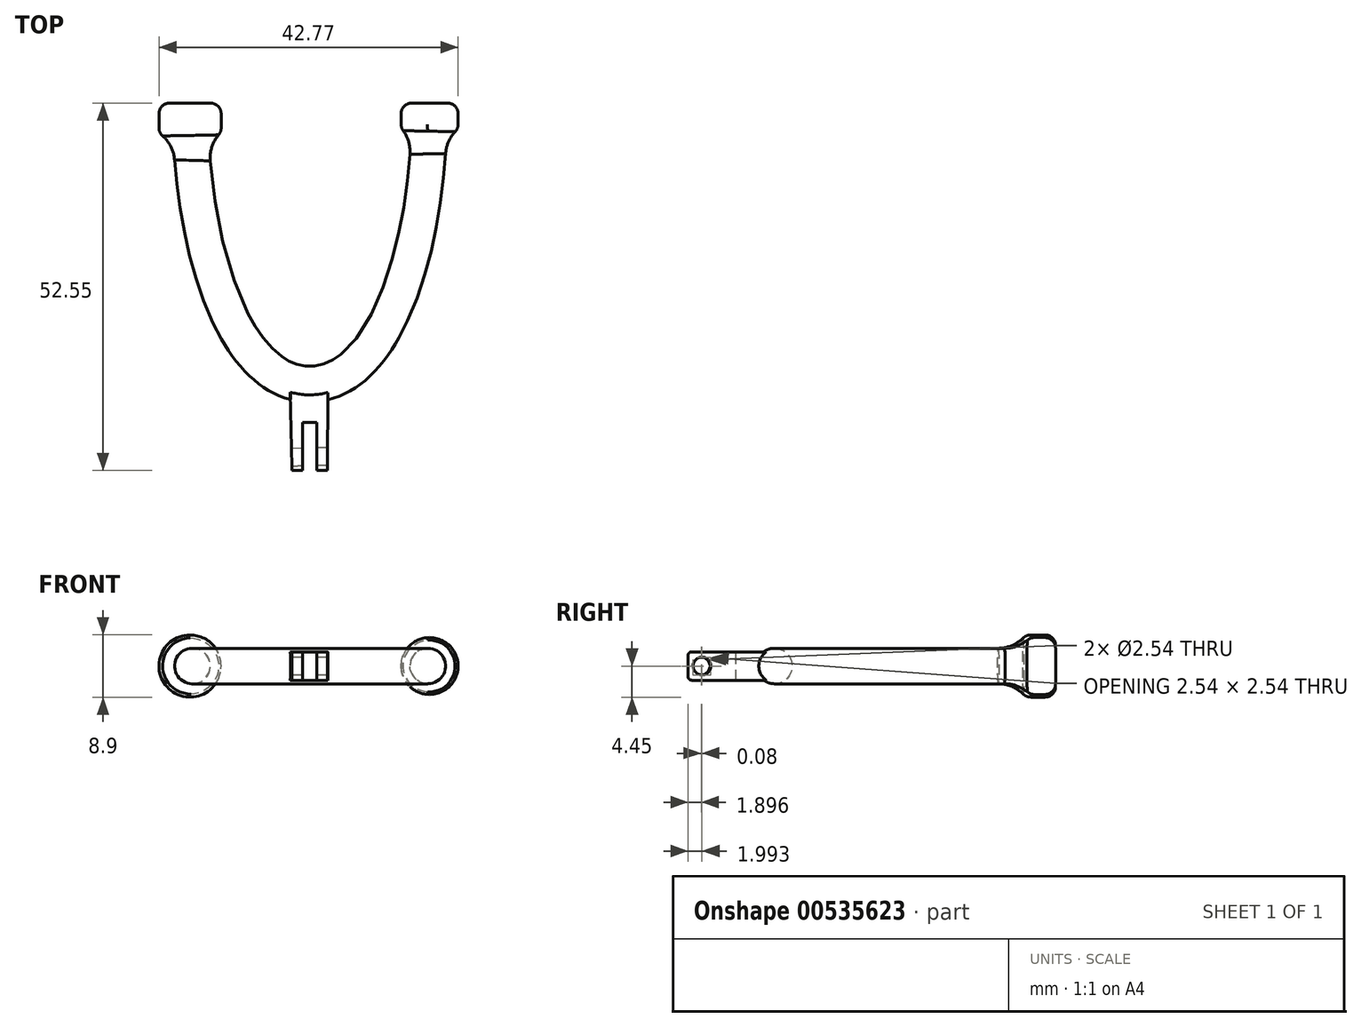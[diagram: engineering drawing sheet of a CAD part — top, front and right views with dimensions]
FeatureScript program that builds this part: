
annotation { "Feature Type Name" : "Feature", "Feature Type Description" : "" }
export const myFeature = defineFeature(function(context is Context, id is Id, definition is map)
    precondition{}
    {
        {
            var Q0;
            Q0=qCreatedBy(makeId("Top.planeOp"),FACE);
            var sketch = newSketch(context, id + "F0", { "sketchPlane" : qUnion([Q0])});
            skLineSegment(sketch, "E0", {"start": v(0, 0) * mm, "end": v(-19.05, 0) * mm, "construction": true});
            skLineSegment(sketch, "E1", {"start": v(0, 0) * mm, "end": v(19.05, 0) * mm, "construction": true});
            skLineSegment(sketch, "E2", {"start": v(24.16, 18.14) * mm, "end": v(-13.94, 18.14) * mm, "construction": true});
            skEllipticalArc(sketch, "E3", {});
            skPoint(sketch, "E3.centerSnap0", {"position": v(5.11, 18.14) * mm});
            const initialGuessF0  = {"E3": [0, 0.01813921518623829, 0, -1, 0.03701277365193682, 0.013935198076069355, 4.71238898038469, 1.5707963267948966]};
            skSetInitialGuess(sketch, initialGuessF0);
            skSolve(sketch);
        }
        {
            var Q0;
            Q0=qCreatedBy(makeId("Front.planeOp"),FACE);
            var Q1;
            Q1=sQuery(id+"F0.wireOp",VERTEX,"E3.end");
            cPlane(context, id + "F1", {"entities" : qUnion([Q0, Q1]), "cplaneType" : CPlaneType.PLANE_POINT, "offset" : 25.4 * mm, "oppositeDirection" : true, "width" : 152.4 * mm, "height" : 152.4 * mm});
        }
        {
            var Q0;
            Q0=qCreatedBy(id+"F1.planeOp",FACE);
            var sketch = newSketch(context, id + "F2", { "sketchPlane" : qUnion([Q0])});
            skCircle(sketch, "E4", {"center": v(-17.13, 0) * mm, "radius": 2.54 * mm});
            skSolve(sketch);
        }
        {
            var Q0;
            Q0=makeQuery(id+"F2.imprint","IMPRINT",FACE,{"disambiguationData":[TD([[makeQuery(id+"F2.imprint","IMPRINT",EDGE,{"derivedFrom":sQuery(id+"F2.wireOp",EDGE,"E4")}),1.0]])]});
            var Q1;
            Q1=sQuery(id+"F0.wireOp",EDGE,"E3");
            sweep(context, id + "F3", {"profiles" : qUnion([Q0]), "path" : qUnion([Q1])});
        }
        {
            var Q0;
            Q0=qCreatedBy(makeId("Top.planeOp"),FACE);
            var sketch = newSketch(context, id + "F4", { "sketchPlane" : qUnion([Q0])});
            skLineSegment(sketch, "E5.0", {"start": v(2.6, -20.26) * mm, "end": v(2.54, -34.4) * mm});
            skLineSegment(sketch, "E6.0", {"start": v(-2.86, -20.23) * mm, "end": v(-2.54, -34.4) * mm});
            skArc(sketch, "E7", {"start": v(-2.86, -20.23) * mm, "mid": v(-0.13, -20.64) * mm, "end": v(2.6, -20.26) * mm});
            skLineSegment(sketch, "E8", {"start": v(-2.54, -34.4) * mm, "end": v(2.54, -34.4) * mm});
            skSolve(sketch);
        }
        {
            var Q0;
            Q0 = qSketchRegion(id + "F4", true);
            extrude(context, id + "F5", {"entities" : qUnion([Q0]), "operationType" : NewBodyOperationType.ADD, "depth" : 2.03 * mm, "offsetDistance" : 25.4 * mm, "hasSecondDirection" : true, "secondDirectionOppositeDirection" : true, "secondDirectionDepth" : 2.03 * mm});
        }
        {
            var Q0;
            Q0=makeQuery(id+"F5.opExtrude","CAP_FACE",FACE,{"disambiguationData":[OSD([sQuery(id+"F4.wireOp",EDGE,"E5.0"),sQuery(id+"F4.wireOp",EDGE,"E6.0"),sQuery(id+"F4.wireOp",EDGE,"E7"),sQuery(id+"F4.wireOp",EDGE,"E8")])],"isStart":false});
            var sketch = newSketch(context, id + "F6", { "sketchPlane" : qUnion([Q0])});
            skLineSegment(sketch, "E9.bottom", {"start": v(1.02, -27.56) * mm, "end": v(-1.02, -27.56) * mm});
            skLineSegment(sketch, "E9.top", {"start": v(1.02, -41.25) * mm, "end": v(-1.02, -41.25) * mm});
            skLineSegment(sketch, "E9.left", {"start": v(1.02, -27.56) * mm, "end": v(1.02, -41.25) * mm});
            skLineSegment(sketch, "E9.right", {"start": v(-1.02, -27.56) * mm, "end": v(-1.02, -41.25) * mm});
            skPoint(sketch, "E9.middle", {"position": v(0, -34.4) * mm});
            skSolve(sketch);
        }
        {
            var Q0;
            Q0 = qSketchRegion(id + "F6", true);
            extrude(context, id + "F7", {"entities" : qUnion([Q0]), "operationType" : NewBodyOperationType.REMOVE, "oppositeDirection" : true, "depth" : 25.4 * mm, "offsetDistance" : 25.4 * mm});
        }
        {
            var Q0;
            Q0=makeQuery(id+"F5.opExtrude","SWEPT_FACE",FACE,{"disambiguationData":[OSD([sQuery(id+"F4.wireOp",EDGE,"E6.0")])]});
            var sketch = newSketch(context, id + "F8", { "sketchPlane" : qUnion([Q0])});
            skCircle(sketch, "E10", {"center": v(450.04, 0) * mm, "radius": 1.27 * mm});
            skCircle(sketch, "E11", {"center": v(32.47, 0) * mm, "radius": 1.27 * mm});
            skSolve(sketch);
        }
        {
            var Q0;
            Q0 = qSketchRegion(id + "F8", true);
            extrude(context, id + "F9", {"entities" : qUnion([Q0]), "operationType" : NewBodyOperationType.REMOVE, "oppositeDirection" : true, "depth" : 25.4 * mm, "offsetDistance" : 25.4 * mm});
        }
        {
            var Q0;
            {var subQ0=sQuery(id+"F4.wireOp",EDGE,"E8");var subQ1=sQuery(id+"F4.wireOp",EDGE,"E6.0");Q0=makeQuery(id+"F7.boolean.opBoolean","SPLIT",EDGE,{"disambiguationData":[TD([makeQuery(id+"F5.opExtrude","SWEPT_FACE",FACE,{"disambiguationData":[OSD([subQ1])]})])],"derivedFrom":makeQuery(id+"F5.opExtrude","CAP_EDGE",EDGE,{"disambiguationData":[OSD([subQ0])],"isStart":false})});}
            var Q1;
            {var subQ0=sQuery(id+"F4.wireOp",EDGE,"E8");var subQ1=sQuery(id+"F4.wireOp",EDGE,"E6.0");Q1=makeQuery(id+"F7.boolean.opBoolean","SPLIT",EDGE,{"disambiguationData":[TD([makeQuery(id+"F5.opExtrude","SWEPT_FACE",FACE,{"disambiguationData":[OSD([subQ1])]})])],"derivedFrom":makeQuery(id+"F5.opExtrude","CAP_EDGE",EDGE,{"disambiguationData":[OSD([subQ0])],"isStart":true})});}
            var Q2;
            {var subQ0=sQuery(id+"F4.wireOp",EDGE,"E5.0");var subQ1=sQuery(id+"F4.wireOp",EDGE,"E8");Q2=makeQuery(id+"F7.boolean.opBoolean","SPLIT",EDGE,{"disambiguationData":[TD([makeQuery(id+"F5.opExtrude","SWEPT_FACE",FACE,{"disambiguationData":[OSD([subQ0])]})])],"derivedFrom":makeQuery(id+"F5.opExtrude","CAP_EDGE",EDGE,{"disambiguationData":[OSD([subQ1])],"isStart":false})});}
            var Q3;
            {var subQ0=sQuery(id+"F4.wireOp",EDGE,"E5.0");var subQ1=sQuery(id+"F4.wireOp",EDGE,"E8");Q3=makeQuery(id+"F7.boolean.opBoolean","SPLIT",EDGE,{"disambiguationData":[TD([makeQuery(id+"F5.opExtrude","SWEPT_FACE",FACE,{"disambiguationData":[OSD([subQ0])]})])],"derivedFrom":makeQuery(id+"F5.opExtrude","CAP_EDGE",EDGE,{"disambiguationData":[OSD([subQ1])],"isStart":true})});}
            fillet(context, id + "F10", {"entities" : qUnion([Q0, Q1, Q2, Q3]), "radius" : 0.5 * mm, "tangentPropagation" : true, "allowEdgeOverflow" : false});
        }
        {
            var Q0;
            Q0=makeQuery(id+"F3.opSweep","CAP_FACE",FACE,{"disambiguationData":[OSD([sQuery(id+"F0.wireOp",VERTEX,"E3.end"),sQuery(id+"F2.wireOp",EDGE,"E4")])],"isStart":false});
            var sketch = newSketch(context, id + "F11", { "sketchPlane" : qUnion([Q0])});
            skCircle(sketch, "E12", {"center": v(-17.13, 0) * mm, "radius": 4.07 * mm});
            skSolve(sketch);
        }
        {
            var Q0;
            Q0 = qSketchRegion(id + "F11", true);
            extrude(context, id + "F12", {"entities" : qUnion([Q0]), "operationType" : NewBodyOperationType.ADD, "oppositeDirection" : true, "depth" : 4.57 * mm, "offsetDistance" : 25.4 * mm});
        }
        {
            var Q0;
            Q0=makeQuery(id+"F3.opSweep","CAP_FACE",FACE,{"disambiguationData":[OSD([sQuery(id+"F0.wireOp",VERTEX,"E3.start"),sQuery(id+"F2.wireOp",EDGE,"E4")])],"isStart":true});
            var sketch = newSketch(context, id + "F13", { "sketchPlane" : qUnion([Q0])});
            skCircle(sketch, "E13", {"center": v(17.13, 0) * mm, "radius": 4.45 * mm});
            skSolve(sketch);
        }
        {
            var Q0;
            Q0 = qSketchRegion(id + "F13", true);
            extrude(context, id + "F14", {"entities" : qUnion([Q0]), "operationType" : NewBodyOperationType.ADD, "oppositeDirection" : true, "depth" : 5.08 * mm, "offsetDistance" : 25.4 * mm});
        }
        {
            var Q0;
            Q0=makeQuery(id+"F14.opExtrude","CAP_EDGE",EDGE,{"disambiguationData":[OSD([sQuery(id+"F13.wireOp",EDGE,"E13")])],"isStart":true});
            var Q1;
            Q1=makeQuery(id+"F14.opExtrude","CAP_EDGE",EDGE,{"disambiguationData":[OSD([sQuery(id+"F13.wireOp",EDGE,"E13")])],"isStart":false});
            var Q2;
            Q2=makeQuery(id+"F12.opExtrude","CAP_EDGE",EDGE,{"disambiguationData":[OSD([sQuery(id+"F11.wireOp",EDGE,"E12")])],"isStart":true});
            var Q3;
            Q3=makeQuery(id+"F12.opExtrude","CAP_EDGE",EDGE,{"disambiguationData":[OSD([sQuery(id+"F11.wireOp",EDGE,"E12")])],"isStart":false});
            fillet(context, id + "F15", {"entities" : qUnion([Q0, Q1, Q2, Q3]), "radius" : 1.52 * mm, "tangentPropagation" : true, "allowEdgeOverflow" : false});
        }
        {
            var Q0;
            Q0=makeQuery(id+"F15.opFillet","BLEND_EDGE",EDGE,{"blendedFrom":[makeQuery(id+"F12.opExtrude","CAP_EDGE",EDGE,{"disambiguationData":[OSD([sQuery(id+"F11.wireOp",EDGE,"E12")])],"isStart":false}),makeQuery(id+"F3.opSweep","SWEPT_FACE",FACE,{"disambiguationData":[OSD([sQuery(id+"F0.wireOp",EDGE,"E3"),sQuery(id+"F2.wireOp",EDGE,"E4")])]})],"blendedInto":[makeQuery(id+"F3.opSweep","SWEPT_FACE",FACE,{"disambiguationData":[OSD([sQuery(id+"F0.wireOp",EDGE,"E3"),sQuery(id+"F2.wireOp",EDGE,"E4")])]})]});
            var Q1;
            Q1=makeQuery(id+"F14.boolean.opBoolean","INTERSECT",EDGE,{"derivedFrom":[makeQuery(id+"F3.opSweep","SWEPT_FACE",FACE,{"disambiguationData":[OSD([sQuery(id+"F0.wireOp",EDGE,"E3"),sQuery(id+"F2.wireOp",EDGE,"E4")])]}),makeQuery(id+"F14.opExtrude","CAP_FACE",FACE,{"disambiguationData":[OSD([sQuery(id+"F13.wireOp",EDGE,"E13")])],"isStart":false})]});
            fillet(context, id + "F16", {"entities" : qUnion([Q0, Q1]), "radius" : 5.08 * mm, "tangentPropagation" : true, "allowEdgeOverflow" : false});
        }
    });
